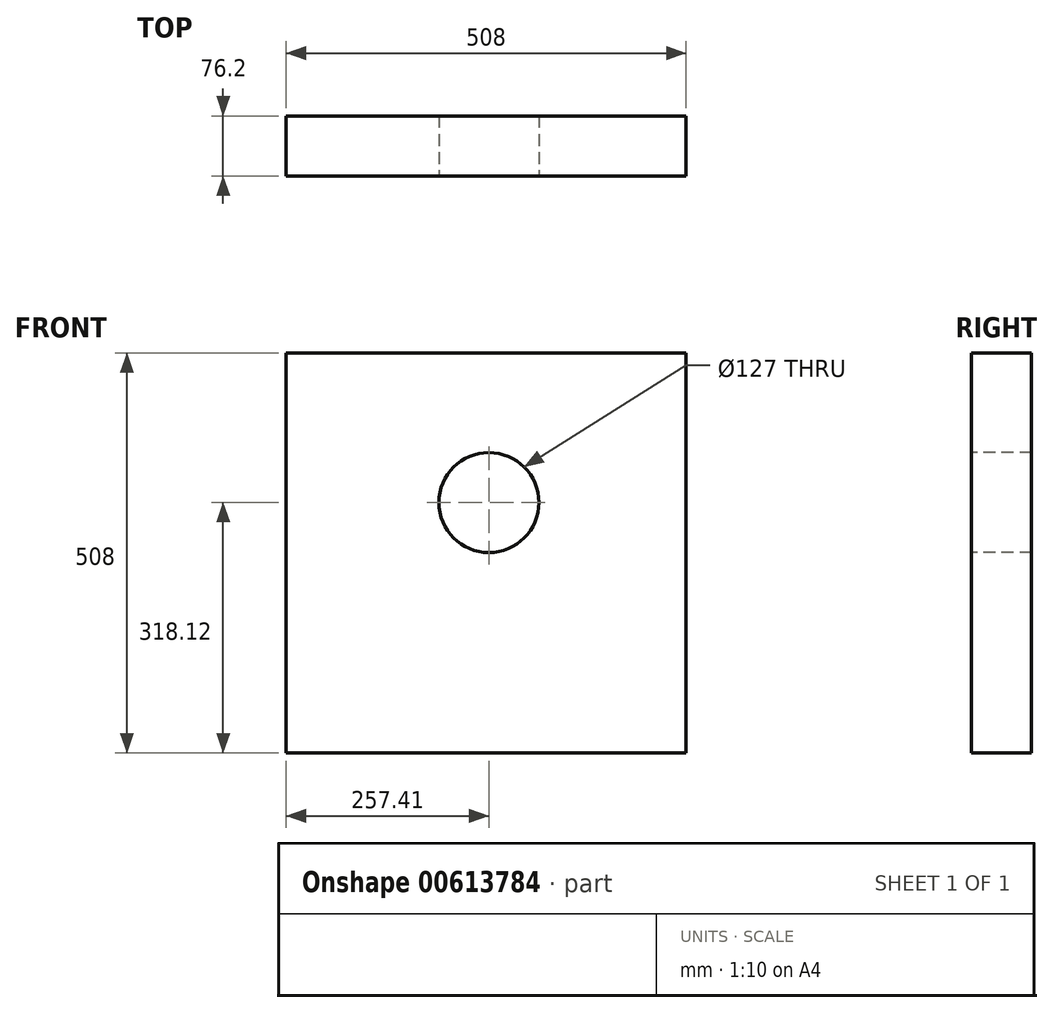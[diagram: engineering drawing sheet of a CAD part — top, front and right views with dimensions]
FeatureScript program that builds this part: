
annotation { "Feature Type Name" : "Feature", "Feature Type Description" : "" }
export const myFeature = defineFeature(function(context is Context, id is Id, definition is map)
    precondition{}
    {
        {
            var Q0;
            Q0=qCreatedBy(makeId("Front.planeOp"),FACE);
            var sketch = newSketch(context, id + "F0", { "sketchPlane" : qUnion([Q0])});
            skLineSegment(sketch, "E0.bottom", {"start": v(-257.41, 354.98) * mm, "end": v(250.59, 354.98) * mm});
            skLineSegment(sketch, "E0.top", {"start": v(-257.41, -153.02) * mm, "end": v(250.59, -153.02) * mm});
            skLineSegment(sketch, "E0.left", {"start": v(-257.41, 354.98) * mm, "end": v(-257.41, -153.02) * mm});
            skLineSegment(sketch, "E0.right", {"start": v(250.59, 354.98) * mm, "end": v(250.59, -153.02) * mm});
            skSolve(sketch);
        }
        {
            var Q0;
            Q0=makeQuery(id+"F0.imprint","IMPRINT",FACE,{"disambiguationData":[TD([[makeQuery(id+"F0.imprint","IMPRINT",EDGE,{"derivedFrom":sQuery(id+"F0.wireOp",EDGE,"E0.bottom")}),-1.0]])]});
            extrude(context, id + "F1", {"entities" : qUnion([Q0]), "depth" : 76.2 * mm, "offsetDistance" : 25.4 * mm});
        }
        {
            var Q0;
            Q0=makeQuery(id+"F1.opExtrude","CAP_FACE",FACE,{"disambiguationData":[OSD([sQuery(id+"F0.wireOp",EDGE,"E0.bottom"),sQuery(id+"F0.wireOp",EDGE,"E0.top"),sQuery(id+"F0.wireOp",EDGE,"E0.left"),sQuery(id+"F0.wireOp",EDGE,"E0.right")])],"isStart":false});
            var sketch = newSketch(context, id + "F2", { "sketchPlane" : qUnion([Q0])});
            skCircle(sketch, "E1", {"center": v(0, 165.1) * mm, "radius": 63.5 * mm});
            skSolve(sketch);
        }
        {
            var Q0;
            Q0=makeQuery(id+"F2.imprint","IMPRINT",FACE,{"disambiguationData":[TD([[makeQuery(id+"F2.imprint","IMPRINT",EDGE,{"derivedFrom":sQuery(id+"F2.wireOp",EDGE,"E1")}),1.0]])]});
            extrude(context, id + "F3", {"entities" : qUnion([Q0]), "operationType" : NewBodyOperationType.REMOVE, "endBound" : BoundingType.UP_TO_NEXT, "oppositeDirection" : true, "depth" : 25.4 * mm, "offsetDistance" : 25.4 * mm});
        }
    });
